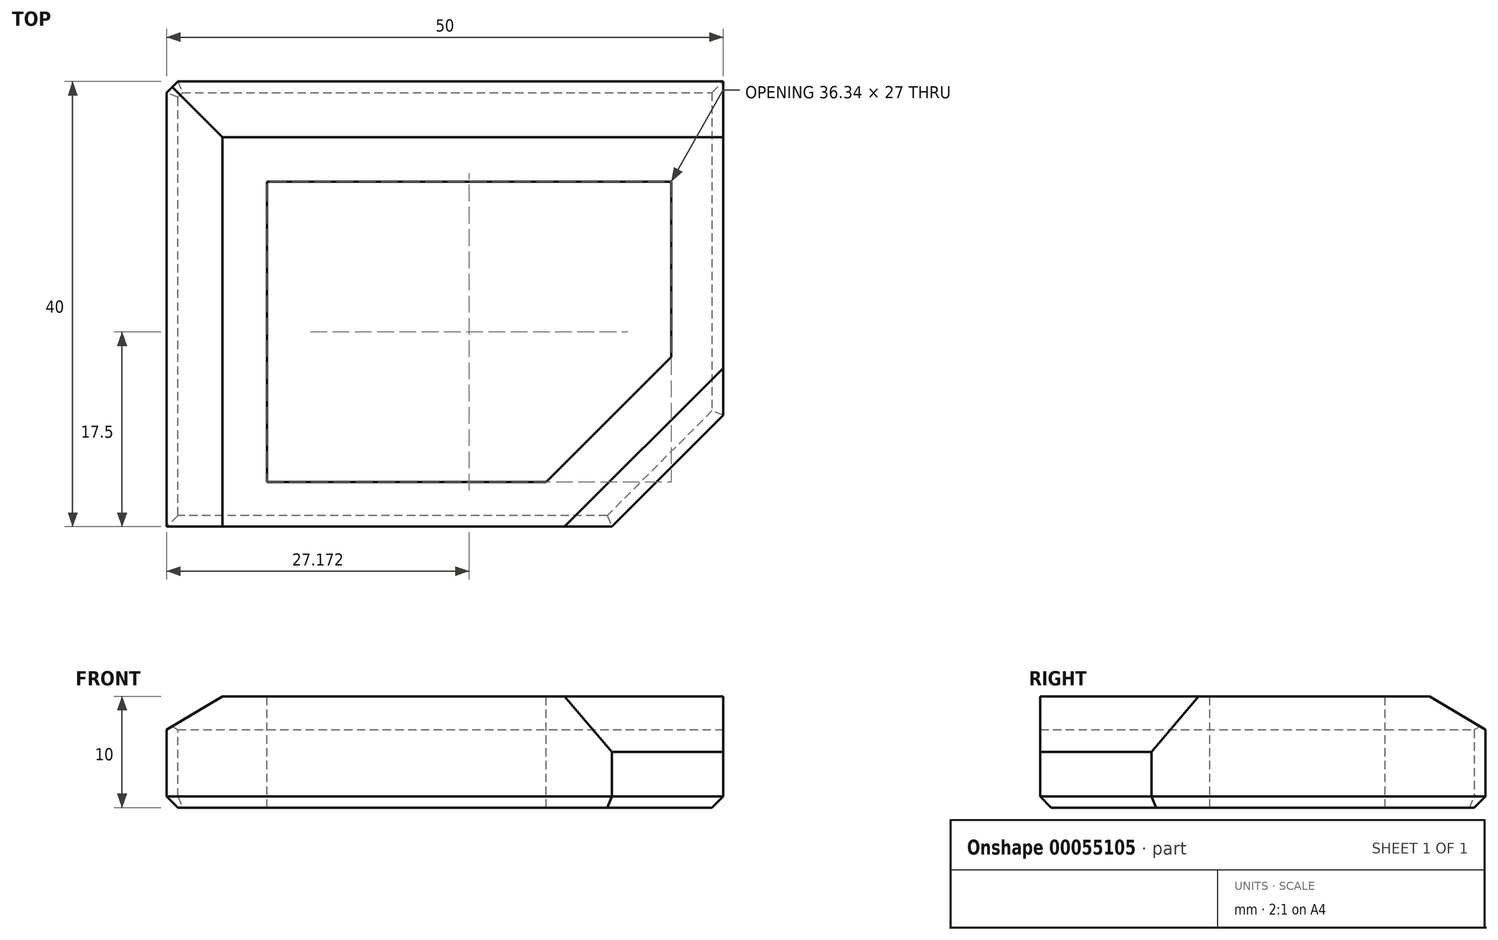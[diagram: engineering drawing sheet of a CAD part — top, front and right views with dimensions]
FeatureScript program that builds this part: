
annotation { "Feature Type Name" : "Feature", "Feature Type Description" : "" }
export const myFeature = defineFeature(function(context is Context, id is Id, definition is map)
    precondition{}
    {
        {
            var Q0;
            Q0=qCreatedBy(makeId("Top.planeOp"),FACE);
            var sketch = newSketch(context, id + "F0", { "sketchPlane" : qUnion([Q0])});
            skLineSegment(sketch, "E0", {"start": v(0, 40) * mm, "end": v(50, 40) * mm});
            skLineSegment(sketch, "E1", {"start": v(50, 40) * mm, "end": v(50, 10) * mm});
            skLineSegment(sketch, "E2", {"start": v(50, 10) * mm, "end": v(40, 0) * mm});
            skLineSegment(sketch, "E3", {"start": v(40, 0) * mm, "end": v(0, 0) * mm});
            skLineSegment(sketch, "E4", {"start": v(0, 0) * mm, "end": v(0, 40) * mm});
            skSolve(sketch);
        }
        {
            var Q0;
            Q0=makeQuery(id+"F0.imprint","IMPRINT",FACE,{"disambiguationData":[TD([[makeQuery(id+"F0.imprint","IMPRINT",EDGE,{"derivedFrom":sQuery(id+"F0.wireOp",EDGE,"E0")}),-1.0]])]});
            extrude(context, id + "F1", {"entities" : qUnion([Q0]), "depth" : 10 * mm});
        }
        {
            var Q0;
            Q0=makeQuery(id+"F1.opExtrude","CAP_EDGE",EDGE,{"disambiguationData":[OSD([sQuery(id+"F0.wireOp",EDGE,"E2")])],"isStart":false});
            chamfer(context, id + "F2", {"entities" : qUnion([Q0]), "chamferType" : ChamferType.TWO_OFFSETS, "width1" : 5 * mm, "oppositeDirection" : false, "width2" : 3 * mm, "tangentPropagation" : true});
        }
        {
            var Q0;
            Q0=makeQuery(id+"F1.opExtrude","SWEPT_EDGE",EDGE,{"disambiguationData":[OSD([sQuery(id+"F0.wireOp",EDGE,"E0"),sQuery(id+"F0.wireOp",EDGE,"E4")])]});
            chamfer(context, id + "F3", {"entities" : qUnion([Q0]), "width" : 1 * mm, "tangentPropagation" : true});
        }
        {
            var Q0;
            Q0=makeQuery(id+"F1.opExtrude","CAP_EDGE",EDGE,{"disambiguationData":[OSD([sQuery(id+"F0.wireOp",EDGE,"E4")])],"isStart":false});
            var Q1;
            Q1=makeQuery(id+"F1.opExtrude","CAP_EDGE",EDGE,{"disambiguationData":[OSD([sQuery(id+"F0.wireOp",EDGE,"E0")])],"isStart":false});
            var Q2;
            {var subQ0=sQuery(id+"F0.wireOp",EDGE,"E4");var subQ1=sQuery(id+"F0.wireOp",EDGE,"E0");Q2=makeQuery(id+"F3.opChamfer","BLEND_EDGE",EDGE,{"blendedFrom":[makeQuery(id+"F1.opExtrude","SWEPT_EDGE",EDGE,{"disambiguationData":[OSD([subQ1,subQ0])]}),makeQuery(id+"F1.opExtrude","CAP_FACE",FACE,{"disambiguationData":[OSD([subQ1,sQuery(id+"F0.wireOp",EDGE,"E1"),sQuery(id+"F0.wireOp",EDGE,"E2"),sQuery(id+"F0.wireOp",EDGE,"E3"),subQ0])],"isStart":false})],"blendedInto":[makeQuery(id+"F1.opExtrude","CAP_FACE",FACE,{"disambiguationData":[OSD([subQ1,sQuery(id+"F0.wireOp",EDGE,"E1"),sQuery(id+"F0.wireOp",EDGE,"E2"),sQuery(id+"F0.wireOp",EDGE,"E3"),subQ0])],"isStart":false})]});}
            chamfer(context, id + "F4", {"entities" : qUnion([Q0, Q1, Q2]), "chamferType" : ChamferType.TWO_OFFSETS, "width1" : 3 * mm, "oppositeDirection" : false, "width2" : 5 * mm, "tangentPropagation" : true});
        }
        {
            var Q0;
            Q0=makeQuery(id+"F1.opExtrude","CAP_FACE",FACE,{"disambiguationData":[OSD([sQuery(id+"F0.wireOp",EDGE,"E0"),sQuery(id+"F0.wireOp",EDGE,"E1"),sQuery(id+"F0.wireOp",EDGE,"E2"),sQuery(id+"F0.wireOp",EDGE,"E3"),sQuery(id+"F0.wireOp",EDGE,"E4")])],"isStart":true});
            chamfer(context, id + "F5", {"entities" : qUnion([Q0]), "width" : 1 * mm, "tangentPropagation" : true});
        }
        {
            var Q0;
            Q0=makeQuery(id+"F1.opExtrude","CAP_FACE",FACE,{"disambiguationData":[OSD([sQuery(id+"F0.wireOp",EDGE,"E0"),sQuery(id+"F0.wireOp",EDGE,"E1"),sQuery(id+"F0.wireOp",EDGE,"E2"),sQuery(id+"F0.wireOp",EDGE,"E3"),sQuery(id+"F0.wireOp",EDGE,"E4")])],"isStart":false});
            var sketch = newSketch(context, id + "F6", { "sketchPlane" : qUnion([Q0])});
            skLineSegment(sketch, "E5", {"start": v(9, 4) * mm, "end": v(34.1, 4) * mm});
            skLineSegment(sketch, "E6", {"start": v(34.1, 4) * mm, "end": v(45.34, 15.24) * mm});
            skLineSegment(sketch, "E7", {"start": v(45.34, 15.24) * mm, "end": v(45.34, 31) * mm});
            skLineSegment(sketch, "E8", {"start": v(45.34, 31) * mm, "end": v(9, 31) * mm});
            skLineSegment(sketch, "E9", {"start": v(9, 31) * mm, "end": v(9, 4) * mm});
            skSolve(sketch);
        }
        {
            var Q0;
            Q0=makeQuery(id+"F6.imprint","IMPRINT",FACE,{"disambiguationData":[TD([[makeQuery(id+"F6.imprint","IMPRINT",EDGE,{"derivedFrom":sQuery(id+"F6.wireOp",EDGE,"E5")}),1.0]])]});
            extrude(context, id + "F7", {"entities" : qUnion([Q0]), "operationType" : NewBodyOperationType.REMOVE, "endBound" : BoundingType.THROUGH_ALL, "oppositeDirection" : true, "depth" : 25 * mm});
        }
    });
